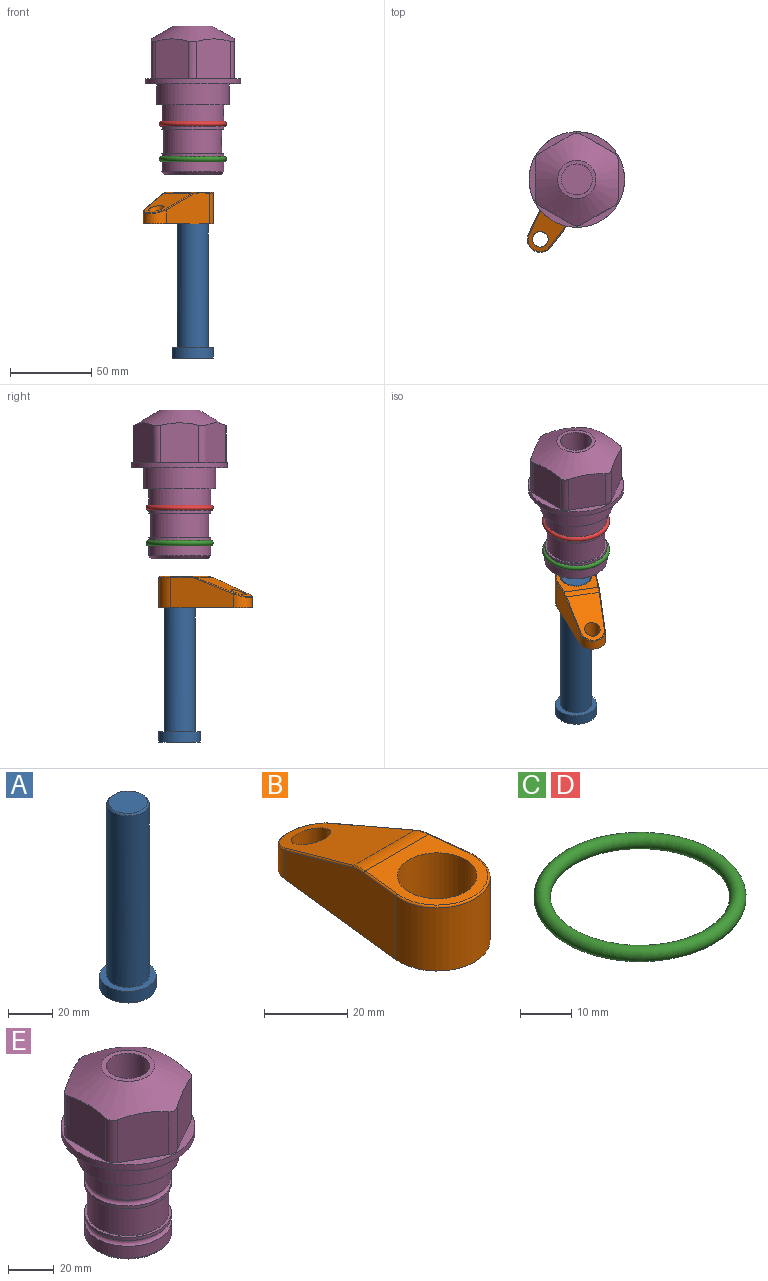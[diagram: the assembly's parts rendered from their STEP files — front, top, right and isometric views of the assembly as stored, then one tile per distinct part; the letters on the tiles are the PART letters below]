
ASSEMBLY  parts=5 mates=3
PART A: 6 faces, bbox 25.4x25.4x101.6 mm
  f0: plane 17.46x17.46mm, normal (0,0,1), area 239.5mm2, adj f5
  f1: plane 25.4x25.4mm, normal (0,0,-1), area 506.7mm2, adj f2
  f2: cylinder r=12.7mm len=25.4mm, axis (0,0,1), area 506.7mm2, adj f1,f3
  f3: plane 25.4x25.4mm, normal (0,0,1), area 221.7mm2, adj f2,f4
  f4: cylinder r=9.53mm len=94.46mm, axis (0,0,1), area 5653mm2, adj f3,f5
  f5: cone r=8.73mm half-angle=45deg, axis (0,0,-1), area 64.4mm2, adj f0,f4
PART B: 44 faces, bbox 27.5x64.5x19.1 mm
  f0: plane 2.3x0.95mm, normal (0,0,-1), area 1mm2, adj f25,f30,f34
  f1: plane 63.5x25.4mm, normal (0,0,-1), area 561.7mm2, adj f2,f3,f4,f5,f6,f7,f19,f20
  f2: cylinder r=12.7mm len=25.4mm, axis (0,0,-1), area 792.2mm2, adj f1,f3,f5,f13
  f3: plane 42.33x18.54mm, normal (0.99,0.11,0), area 647mm2, adj f1,f2,f4,f11,f12,f14
  f4: cylinder r=7.94mm len=15.78mm, axis (0,0,-1), area 158.6mm2, adj f1,f3,f5,f16
  f5: plane 42.33x18.54mm, normal (-0.99,0.11,0), area 647mm2, adj f1,f2,f4,f15,f17,f18
  f6: cylinder r=9.53mm len=19.05mm, axis (0,0,-1), area 1140.1mm2, adj f1,f8
  f7: cylinder r=4.76mm len=10.98mm, axis (0,0,-1), area 276.1mm2, adj f1,f9
  f8: plane 25.83x24.38mm, normal (0,0,1), area 262.2mm2, adj f6,f10,f11,f13,f15
  f9: plane 32.49x20.55mm, normal (0,0.34,0.94), area 489.9mm2, adj f7,f10,f14,f16,f18
  f10: cylinder r=12.7mm len=21.49mm, axis (-1,0,0), area 93.2mm2, adj f8,f9,f12,f17
  f11: cylinder r=0.51mm len=12.34mm, axis (0.11,-0.99,0), area 9.9mm2, adj f3,f8,f12,f13
  f12: bspline ~7.62x1.64mm, area 3.5mm2, adj f3,f10,f11,f14
  f13: torus R=12.19mm, axis (0,0,1), area 33.6mm2, adj f2,f8,f11,f15
  f14: cylinder r=0.51mm len=26.01mm, axis (0.1,-0.93,0.34), area 21.6mm2, adj f3,f9,f12,f16
  f15: cylinder r=0.51mm len=12.34mm, axis (0.11,0.99,0), area 9.9mm2, adj f5,f8,f13,f17
  f16: bspline ~15.78x7.05mm, area 15.7mm2, adj f4,f9,f14,f18
  f17: bspline ~7.62x1.64mm, area 3.5mm2, adj f5,f10,f15,f18
  f18: cylinder r=0.51mm len=26.01mm, axis (0.1,0.93,-0.34), area 21.6mm2, adj f5,f9,f16,f17
  f19: plane 21.6x14.29mm, normal (-0.99,-0.11,0), area 242.6mm2, adj f1,f26,f28,f34,f36,f38
  f20: plane 21.6x14.29mm, normal (0.99,-0.11,0), area 242.6mm2, adj f1,f27,f29,f37,f39,f41
  f21: cylinder r=12.7mm len=14.29mm, axis (0,0,-1), area 173.2mm2, adj f1,f26,f27,f30,f31,f33
  f22: cylinder r=7.94mm len=7.63mm, axis (0,0,-1), area 53.8mm2, adj f1,f28,f29,f42
  f23: plane 2.3x0.95mm, normal (0,0,-1), area 1mm2, adj f25,f33,f37
  f24: plane 17.94x12.32mm, normal (0,-0.34,-0.94), area 191.2mm2, adj f25,f38,f41,f42
  f25: cylinder r=9.53mm len=12.93mm, axis (-1,0,0), area 37.5mm2, adj f0,f23,f24,f31,f36,f39
  f26: cylinder r=1.59mm len=14.29mm, axis (0,0,-1), area 49mm2, adj f1,f19,f21,f32
  f27: cylinder r=1.59mm len=14.29mm, axis (0,0,-1), area 49mm2, adj f1,f20,f21,f35
  f28: cylinder r=1.59mm len=7.28mm, axis (0,0,-1), area 22.1mm2, adj f1,f19,f22,f40
  f29: cylinder r=1.59mm len=7.28mm, axis (0,0,-1), area 22.1mm2, adj f1,f20,f22,f43
  f30: torus R=14.29mm, axis (0,0,1), area 5.8mm2, adj f0,f21,f31,f32
  f31: bspline ~11.06x2.73mm, area 20.8mm2, adj f21,f25,f30,f33
  f32: sphere r=1.59mm, area 5.4mm2, adj f26,f30,f34
  f33: torus R=14.29mm, axis (0,0,1), area 5.8mm2, adj f21,f23,f31,f35
  f34: cylinder r=1.59mm len=1.68mm, axis (-0.11,0.99,0), area 2.4mm2, adj f0,f19,f32,f36
  f35: sphere r=1.59mm, area 5.4mm2, adj f27,f33,f37
  f36: bspline ~5.82x2.33mm, area 7.7mm2, adj f19,f25,f34,f38
  f37: cylinder r=1.59mm len=1.68mm, axis (0.11,0.99,0), area 2.4mm2, adj f20,f23,f35,f39
  f38: cylinder r=1.59mm len=18.33mm, axis (0.1,-0.93,0.34), area 46.7mm2, adj f19,f24,f36,f40
  f39: bspline ~5.82x2.33mm, area 7.7mm2, adj f20,f25,f37,f41
  f40: sphere r=1.59mm, area 3.6mm2, adj f28,f38,f42
  f41: cylinder r=1.59mm len=18.33mm, axis (0.1,0.93,-0.34), area 46.7mm2, adj f20,f24,f39,f43
  f42: bspline ~8.31x1.84mm, area 15.3mm2, adj f22,f24,f40,f43
  f43: sphere r=1.59mm, area 3.6mm2, adj f29,f41,f42
PART C: 1 faces, bbox 44.7x44.7x3.2 mm
  f0: torus R=19.05mm, axis (0,0,1), area 1193.9mm2
PART D: same geometry as C
PART E: 36 faces, bbox 58.7x58.7x91.2 mm
  f0: cylinder r=17.78mm len=35.56mm, axis (0,0,1), area 1670.8mm2, adj f23,f24,f31
  f1: cylinder r=19.05mm len=38.1mm, axis (0,0,1), area 1191.9mm2, adj f26,f27,f30
  f2: plane 58.66x58.66mm, normal (0,0,-1), area 1150.6mm2, adj f3,f28
  f3: cylinder r=29.33mm len=58.66mm, axis (0,0,-1), area 585.1mm2, adj f2,f4
  f4: plane 58.66x58.66mm, normal (0,0,1), area 475.9mm2, adj f3,f5,f6,f7,f8,f9,f10,f11
  f5: plane 24.5x20.32mm, normal (-0.5,0.87,0), area 562.8mm2, adj f4,f15,f16,f17
  f6: plane 24.5x20.32mm, normal (0.5,0.87,0), area 562.8mm2, adj f4,f14,f15,f17
  f7: plane 24.5x23.48mm, normal (1,0,0), area 562.8mm2, adj f4,f13,f14,f17
  f8: plane 24.5x20.32mm, normal (0.5,-0.87,0), area 562.8mm2, adj f4,f12,f13,f17
  f9: plane 24.5x20.32mm, normal (-0.5,-0.87,0), area 562.8mm2, adj f4,f11,f12,f17
  f10: plane 24.5x23.48mm, normal (-1,0,0), area 562.8mm2, adj f4,f11,f16,f17
  f11: cylinder r=5.08mm len=23.01mm, axis (0,0,-1), area 121.2mm2, adj f4,f9,f10,f17
  f12: cylinder r=5.08mm len=23.01mm, axis (0,0,-1), area 121.2mm2, adj f4,f8,f9,f17
  f13: cylinder r=5.08mm len=23.01mm, axis (0,0,-1), area 121.2mm2, adj f4,f7,f8,f17
  f14: cylinder r=5.08mm len=23.01mm, axis (0,0,-1), area 121.2mm2, adj f4,f6,f7,f17
  f15: cylinder r=5.08mm len=23.01mm, axis (0,0,-1), area 121.2mm2, adj f4,f5,f6,f17
  f16: cylinder r=5.08mm len=23.01mm, axis (0,0,-1), area 121.2mm2, adj f4,f5,f10,f17
  f17: cone r=11.73mm half-angle=60deg, axis (0,0,-1), area 2071.8mm2, adj f5,f6,f7,f8,f9,f10,f11,f12
  f18: plane 23.46x23.46mm, normal (0,0,1), area 147.4mm2, adj f17,f35
  f19: plane 34.93x34.93mm, normal (0,0,-1), area 958mm2, adj f29
  f20: cylinder r=19.05mm len=38.1mm, axis (0,0,1), area 760.1mm2, adj f21,f29
  f21: torus R=19.05mm, axis (0,0,1), area 565.3mm2, adj f20,f22
  f22: cylinder r=19.05mm len=38.1mm, axis (0,0,1), area 190mm2, adj f21,f23
  f23: plane 38.1x38.1mm, normal (0,0,1), area 146.9mm2, adj f0,f22
  f24: plane 38.1x38.1mm, normal (0,0,-1), area 146.9mm2, adj f0,f25
  f25: cylinder r=19.05mm len=38.1mm, axis (0,0,1), area 190mm2, adj f24,f26
  f26: torus R=19.05mm, axis (0,0,1), area 565.3mm2, adj f1,f25
  f27: plane 44.45x44.45mm, normal (0,0,-1), area 411.7mm2, adj f1,f28
  f28: cylinder r=22.23mm len=44.45mm, axis (0,0,1), area 1773.5mm2, adj f2,f27
  f29: cone r=19.05mm half-angle=45deg, axis (0,0,1), area 257.5mm2, adj f19,f20
  f30: cylinder r=3.17mm len=6.75mm, axis (-1,0,0), area 128mm2, adj f1,f33
  f31: cylinder r=3.17mm len=6.35mm, axis (-1,0,0), area 102.5mm2, adj f0,f33
  f32: plane 25.4x25.4mm, normal (0,0,1), area 506.7mm2, adj f33
  f33: cylinder r=12.7mm len=66.42mm, axis (0,0,-1), area 5236.2mm2, adj f30,f31,f32,f34
  f34: cone r=9.53mm half-angle=30deg, axis (0,0,-1), area 443.4mm2, adj f33,f35
  f35: cylinder r=9.53mm len=19.05mm, axis (0,0,-1), area 849mm2, adj f18,f34
PLACE A rot(axis=(0,0,-1),121.5deg) t=(0,0,-140.28)mm
PLACE B rot(axis=(0,0,1),148.5deg) t=(0,0,-85.67)mm
PLACE C t=(0,0,-21.59)mm
PLACE D at identity
PLACE E at identity fixed
MATE fastened C.f0 <-> E.f0  axis (0,0,1) through (0,0,-46.1)mm
MATE cylindrical A.f2 <-> E.f0  axis (0,0,1) through (0,0,-114.65)mm
MATE fastened B.f2 <-> A.f2  axis (0,0,1) through (0,0,-66.62)mm
